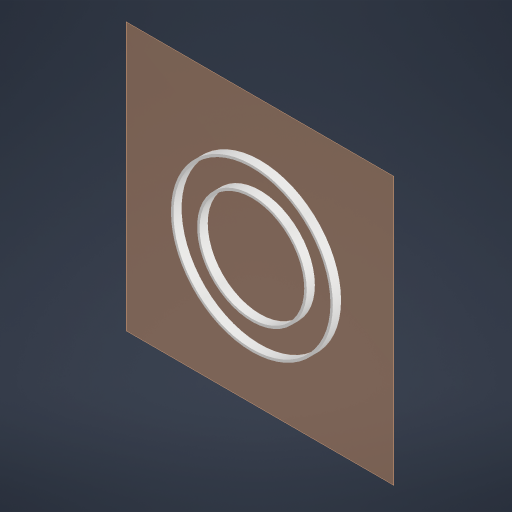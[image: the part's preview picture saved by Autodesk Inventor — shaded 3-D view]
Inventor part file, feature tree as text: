
AUTODESK INVENTOR PART (.ipt)
format: ipt  version: 2023.1 (Build 271208000, 208)  size: 191,488 bytes
history: native  units: mm
features: other x3, plane x2, extrude x2, sketch x2
ambient origin geometry x8: Origin, YZ Plane, XZ Plane, XY Plane, X Axis, Y Axis, Z Axis, Center Point
bodies: Solid1 (feature_tree)
feature tree (9):
  plane  "Work Plane1"
  extrude  "Extrusion1"  Depth=3.0mm
  plane  "Work Plane2"
  extrude  "Extrusion2"  Depth=10.0mm
  sketch  "Sketch1"  dims[d0=190.985932mm d1=3.0mm]
  sketch  "Sketch2"  dims[d2=10.0mm d3=0.0mm d4=127.323954mm d5=3.0mm d6=10.0mm d7=0.0mm]
  parser-record x1  (decoder bookkeeping rows leaked as tree rows — omitted from the tree; the rows remain in map.json)
  other  "Beau4tClock.iam"
  other  "Clock:1"
note: 1 file-system path scrubbed to <path> (originals preserved in map.json)
